# Revit family: URBANE II HAND WALL BASIN 1TH NOF
name_source: partatom
category: Specialty Equipment
units: mm (PartAtom-declared; Revit-internal decimal feet)

## family parameters
Cut with Voids When Loaded = Yes
Host = Face
OmniClass Number = 23.45.05.14.14
OmniClass Title = Sinks/Lavatories
Part Type = Normal
Room Calculation Point = No
Round Connector Dimension = Use Radius
Shared = No

## types (1)
- URBANE II HAND WALL BASIN 1TH NOF
    Assembly Code = D2010400
    Default Elevation = 900 mm  [stored 2.95276 ft]
    Description = URBANE II HAND WALL BASIN 1TH NOF
    Manufacturer = GWA Bathrooms & Kitchens
    Material_Base = GWA-Porcelain-White
    Model = 879010W
    TapHole = Yes
    TapHoleCutout = -50 mm  [stored -0.164042 ft]
    URL = https://www.caroma.com.au

note: [stored X ft] marks values corroborated as IEEE doubles in the binary element streams (Revit-internal decimal feet)

## geometry (parser evidence)
native form markers: Sweep x2
no freeform markers — native parametric forms only
